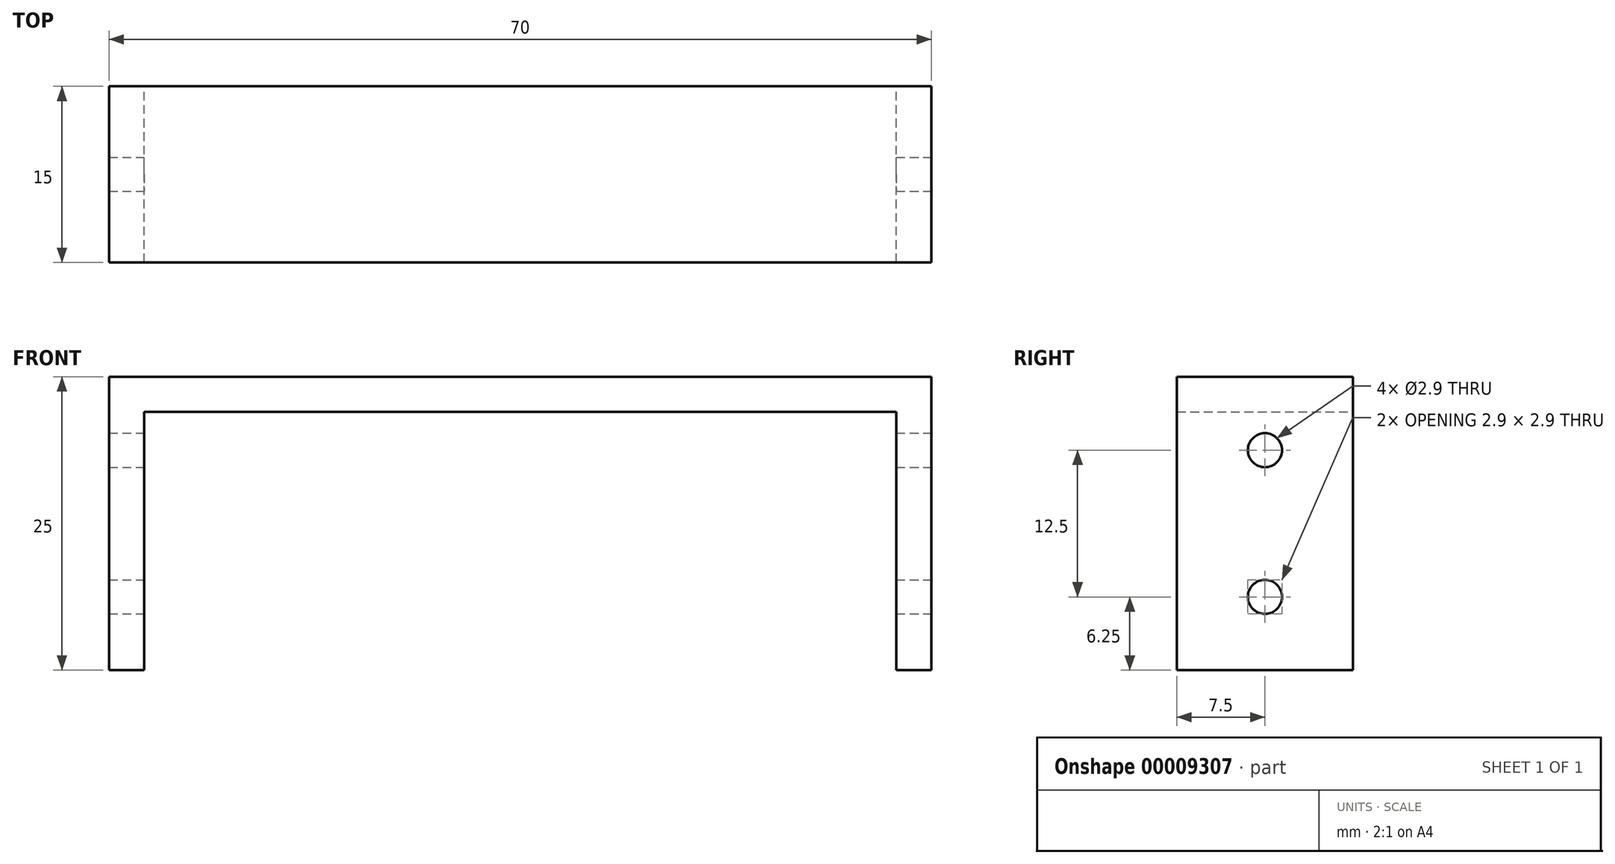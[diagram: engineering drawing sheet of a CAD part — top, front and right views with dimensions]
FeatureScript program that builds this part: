
annotation { "Feature Type Name" : "Feature", "Feature Type Description" : "" }
export const myFeature = defineFeature(function(context is Context, id is Id, definition is map)
    precondition{}
    {
        {
            var Q0;
            Q0=qCreatedBy(makeId("Front.planeOp"),FACE);
            var sketch = newSketch(context, id + "F0", { "sketchPlane" : qUnion([Q0])});
            skLineSegment(sketch, "E0", {"start": v(0, 0) * mm, "end": v(35, 0) * mm});
            skLineSegment(sketch, "E1", {"start": v(35, 0) * mm, "end": v(35, -25) * mm});
            skLineSegment(sketch, "E2", {"start": v(35, -25) * mm, "end": v(32, -25) * mm});
            skLineSegment(sketch, "E3", {"start": v(32, -25) * mm, "end": v(32, -3) * mm});
            skLineSegment(sketch, "E4", {"start": v(32, -3) * mm, "end": v(0, -3) * mm});
            skLineSegment(sketch, "E5.0.MirrorCS", {"start": v(0, 0) * mm, "end": v(-35, 0) * mm});
            skLineSegment(sketch, "E6.0.MirrorCS", {"start": v(-35, 0) * mm, "end": v(-35, -25) * mm});
            skLineSegment(sketch, "E7.0.MirrorCS", {"start": v(-35, -25) * mm, "end": v(-32, -25) * mm});
            skLineSegment(sketch, "E8.0.MirrorCS", {"start": v(-32, -25) * mm, "end": v(-32, -3) * mm});
            skLineSegment(sketch, "E9.0.MirrorCS", {"start": v(-32, -3) * mm, "end": v(0, -3) * mm});
            skSolve(sketch);
        }
        {
            var Q0;
            Q0=makeQuery(id+"F0.imprint","IMPRINT",FACE,{"disambiguationData":[TD([[makeQuery(id+"F0.imprint","IMPRINT",EDGE,{"derivedFrom":sQuery(id+"F0.wireOp",EDGE,"E0")}),-1.0]])]});
            extrude(context, id + "F1", {"entities" : qUnion([Q0]), "depth" : 15 * mm});
        }
        {
            var Q0;
            Q0=makeQuery(id+"F1.opExtrude","SWEPT_FACE",FACE,{"disambiguationData":[OSD([sQuery(id+"F0.wireOp",EDGE,"E1")])]});
            var sketch = newSketch(context, id + "F2", { "sketchPlane" : qUnion([Q0])});
            skLineSegment(sketch, "E10", {"start": v(-7.5, 0) * mm, "end": v(-7.5, -12.5) * mm, "construction": true});
            skCircle(sketch, "E11", {"center": v(-7.5, -6.25) * mm, "radius": 1.45 * mm});
            skLineSegment(sketch, "E12", {"start": v(-15, -12.5) * mm, "end": v(0, -12.5) * mm, "construction": true});
            skLineSegment(sketch, "E13", {"start": v(-7.5, -12.5) * mm, "end": v(-7.5, -25) * mm, "construction": true});
            skCircle(sketch, "E14.0.MirrorC", {"center": v(-7.5, -18.75) * mm, "radius": 1.45 * mm});
            skSolve(sketch);
        }
        {
            var Q0;
            Q0 = qSketchRegion(id + "F2", true);
            extrude(context, id + "F3", {"entities" : qUnion([Q0]), "operationType" : NewBodyOperationType.REMOVE, "endBound" : BoundingType.THROUGH_ALL, "oppositeDirection" : true, "depth" : 25 * mm});
        }
    });
